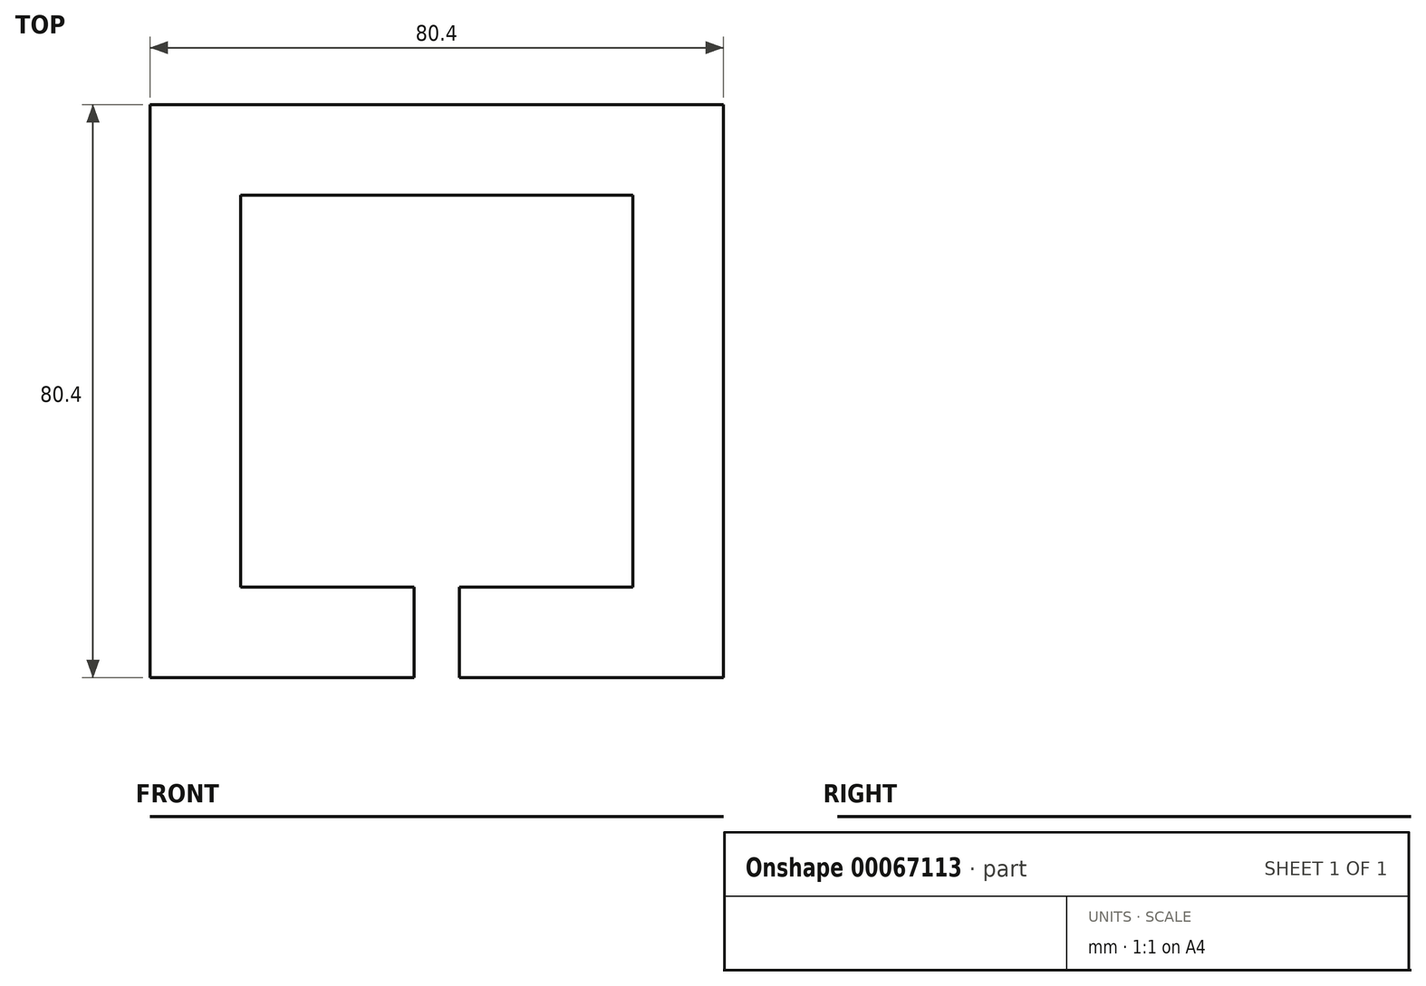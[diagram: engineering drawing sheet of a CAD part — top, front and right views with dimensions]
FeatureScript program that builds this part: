
annotation { "Feature Type Name" : "Feature", "Feature Type Description" : "" }
export const myFeature = defineFeature(function(context is Context, id is Id, definition is map)
    precondition{}
    {
        {
            var Q0;
            Q0=qCreatedBy(makeId("Top.planeOp"),FACE);
            var sketch = newSketch(context, id + "F0", { "sketchPlane" : qUnion([Q0])});
            skLineSegment(sketch, "E0.bottom", {"start": v(-40.2, 0) * mm, "end": v(40.2, 0) * mm});
            skLineSegment(sketch, "E0.top", {"start": v(-40.2, -80.4) * mm, "end": v(40.2, -80.4) * mm});
            skLineSegment(sketch, "E0.left", {"start": v(-40.2, 0) * mm, "end": v(-40.2, -80.4) * mm});
            skLineSegment(sketch, "E0.right", {"start": v(40.2, 0) * mm, "end": v(40.2, -80.4) * mm});
            skLineSegment(sketch, "E1.bottom", {"start": v(-27.5, -12.7) * mm, "end": v(27.5, -12.7) * mm});
            skLineSegment(sketch, "E1.top", {"start": v(-27.5, -67.7) * mm, "end": v(27.5, -67.7) * mm});
            skLineSegment(sketch, "E1.left", {"start": v(-27.5, -12.7) * mm, "end": v(-27.5, -67.7) * mm});
            skLineSegment(sketch, "E1.right", {"start": v(27.5, -12.7) * mm, "end": v(27.5, -67.7) * mm});
            skLineSegment(sketch, "E2", {"start": v(-27.5, -12.7) * mm, "end": v(-40.2, -12.7) * mm, "construction": true});
            skLineSegment(sketch, "E3", {"start": v(27.5, -12.7) * mm, "end": v(40.2, -12.7) * mm, "construction": true});
            skLineSegment(sketch, "E4", {"start": v(0, 0) * mm, "end": v(0, -12.7) * mm, "construction": true});
            skLineSegment(sketch, "E5.bottom", {"start": v(-3.18, -67.7) * mm, "end": v(3.18, -67.7) * mm});
            skLineSegment(sketch, "E5.top", {"start": v(-3.17, -80.4) * mm, "end": v(3.17, -80.4) * mm});
            skLineSegment(sketch, "E5.left", {"start": v(-3.17, -67.7) * mm, "end": v(-3.17, -80.4) * mm});
            skLineSegment(sketch, "E5.right", {"start": v(3.18, -67.7) * mm, "end": v(3.18, -80.4) * mm});
            skLineSegment(sketch, "E6", {"start": v(-3.18, -74.05) * mm, "end": v(-40.2, -74.05) * mm, "construction": true});
            skLineSegment(sketch, "E7", {"start": v(3.18, -74.05) * mm, "end": v(40.2, -74.05) * mm, "construction": true});
            skSolve(sketch);
        }
        {
            var Q0;
            Q0=makeQuery(id+"F0.imprint","IMPRINT",FACE,{"disambiguationData":[TD([[makeQuery(id+"F0.imprint","IMPRINT",EDGE,{"derivedFrom":sQuery(id+"F0.wireOp",EDGE,"E0.bottom")}),-1.0]])]});
            extrude(context, id + "F1", {"entities" : qUnion([Q0]), "depth" : 1 / 203.2 * mm});
        }
    });
